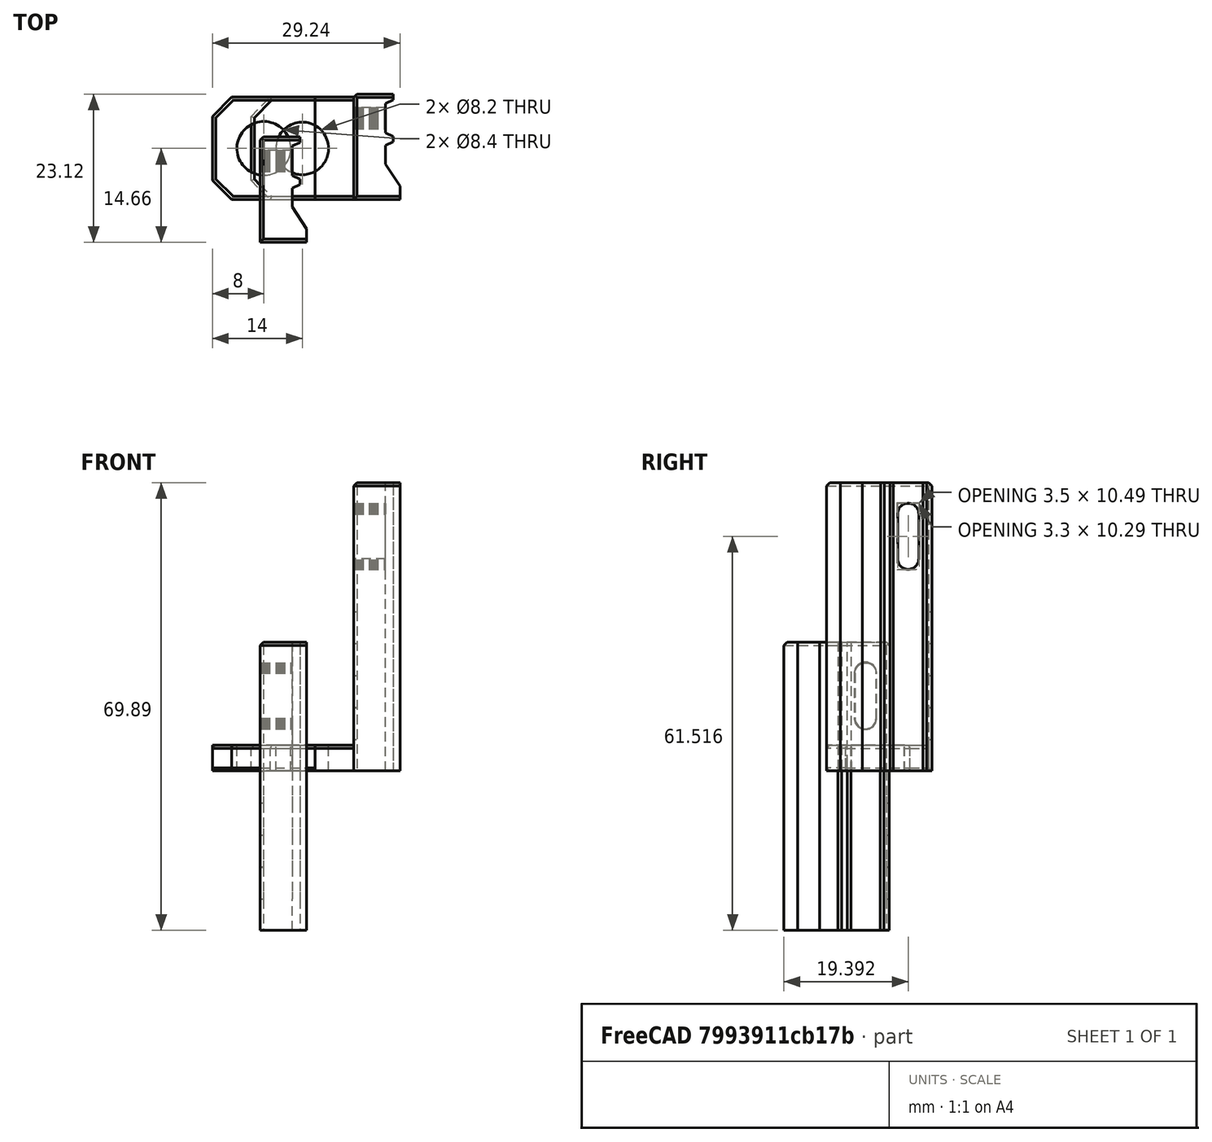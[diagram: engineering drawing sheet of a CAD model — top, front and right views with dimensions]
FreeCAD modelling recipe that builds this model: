
FCSTD DOCUMENT  (FreeCAD 0.18R14555 (Git shallow))
Label: pinda-probe-mount
License: All rights reserved
LicenseURL: http://en.wikipedia.org/wiki/All_rights_reserved
objects: Part::Feature×11, Part::Box×4, Part::Chamfer×4, Part::Cut×3, Part::MultiFuse×2, Part::Cylinder×2, Mesh::Feature×1, Part::MultiCommon×1
note: 27 computed .brp shape members not serialized (recipe doc carries the construction recipe); baked Part::Feature solids carry a one-line shape summary decoded from their .brp

FEATURE [Mesh::Feature] adj_bltouch_mount_4A_wing_1_  label="adj-bltouch-mount-4A-wing(1)"
FEATURE [Part::Feature] adj_bltouch_mount_4A_wing_1_001
  shape: bbox 32.68 x 16.46 x 20.13 mm, 1526 faces, 0 solids (baked)
FEATURE [Part::Feature] adj_bltouch_mount_4A_wing_1_001_solid  label="adj_bltouch_mount_4A_wing_1_001 (Solid)"
  Placement = pos=(-68,32,19) rot=(0,0,1;0rad)
  shape: bbox 32.68 x 16.46 x 20.13 mm, 1526 faces (baked)
FEATURE [Part::Box] Box  label="Cube"
  AttacherType = Attacher::AttachEngine3D
  Height = 45
  Length = 37
  Placement = pos=(5.44,0,-4) rot=(0,0,1;0rad)
  Width = 35
FEATURE [Part::Cut] Cut
  Base = -> adj_bltouch_mount_4A_wing_1_001_solid
  Placement = pos=(-41,-15,0) rot=(0,0,1;0rad)
  Tool = -> Box
FEATURE [Part::Feature] Cut001
  Placement = pos=(-41,-15,0) rot=(0,0,1;0rad)
  shape: bbox 7.237 x 16.46 x 20.13 mm, 335 faces (baked)
FEATURE [Part::Box] Box001  label="Cube001"
  AttacherType = Attacher::AttachEngine3D
  Height = 6
  Length = 11
  Placement = pos=(0,-9,0) rot=(0,0,1;0rad)
  Width = 20
FEATURE [Part::MultiCommon] Common
  Placement = pos=(0,0,-5) rot=(0,0,1;0rad)
  Shapes = -> [Cut001,Box001]
FEATURE [Part::Feature] Common001
  Placement = pos=(0,0,-10) rot=(0,0,1;0rad)
  shape: bbox 7.237 x 16.46 x 6 mm, 54 faces (baked)
FEATURE [Part::Feature] Common002
  Placement = pos=(0,0,-15) rot=(0,0,1;0rad)
  shape: bbox 7.237 x 16.46 x 6 mm, 54 faces (baked)
FEATURE [Part::Feature] Common003
  Placement = pos=(0,0,-20) rot=(0,0,1;0rad)
  shape: bbox 7.237 x 16.46 x 6 mm, 54 faces (baked)
FEATURE [Part::Feature] Common005
  Placement = pos=(0,0,-24.89) rot=(0,0,1;0rad)
  shape: bbox 7.237 x 16.46 x 6 mm, 54 faces (baked)
FEATURE [Part::MultiFuse] Fusion
  Shapes = -> [Cut,Common002,Common005,Common001,Common003,Common]
FEATURE [Part::Box] Box003  label="Cube003"
  AttacherType = Attacher::AttachEngine3D
  Height = 4
  Length = 16
  Placement = pos=(-6,0,0) rot=(0,0,1;0rad)
  Width = 16
FEATURE [Part::Cylinder] Cylinder
  Angle = 360
  AttacherType = Attacher::AttachEngine3D
  Height = 4
  Placement = pos=(2,8,0) rot=(0,0,1;0rad)
  Radius = 4.2
FEATURE [Part::Cut] Cut003
  Base = -> Box003
  Tool = -> Cylinder
FEATURE [Part::Chamfer] Chamfer
  Base = -> Cut003
  Edges = 2 edges r=3: [Edge1,Edge3]
FEATURE [Part::Feature] Chamfer001
  shape: bbox 16 x 16 x 4 mm, 9 faces (baked)
FEATURE [Part::Chamfer] Chamfer002
  Base = -> Chamfer001
  Edges = 9 edges r=0.5: [Edge1,Edge4,Edge5,Edge6,Edge7,Edge8,Edge11,Edge13,Edge15]
FEATURE [Part::Feature] Fusion001
  Placement = pos=(14.56,6.66,24.89) rot=(0,0,1;0rad)
  shape: bbox 7.237 x 16.46 x 45 mm, 180 faces (baked)
FEATURE [Part::Box] Box004  label="Cube004"
  AttacherType = Attacher::AttachEngine3D
  Height = 4
  Length = 16
  Width = 16
FEATURE [Part::Cylinder] Cylinder001
  Angle = 360
  AttacherType = Attacher::AttachEngine3D
  Height = 4
  Placement = pos=(8,8,0) rot=(0,0,1;0rad)
  Radius = 4.1
FEATURE [Part::Cut] Cut004
  Base = -> Box004
  Tool = -> Cylinder001
FEATURE [Part::Chamfer] Chamfer003
  Base = -> Cut004
  Edges = 2 edges r=3: [Edge1,Edge3]
FEATURE [Part::Chamfer] Chamfer004
  Base = -> Chamfer003
  Edges = 5 edges r=0.5: [Edge1,Edge5,Edge6,Edge7,Edge8]
FEATURE [Part::MultiFuse] Fusion002
  Shapes = -> [Chamfer004,Fusion001]
FEATURE [Part::Feature] Fusion002001  label="Fusion003"
  shape: bbox 23.24 x 16.46 x 45 mm, 194 faces (baked)
FEATURE [Part::Feature] Fusion002001_solid  label="Fusion003 (Solid)"
  shape: bbox 23.24 x 16.46 x 45 mm, 194 faces (baked)
